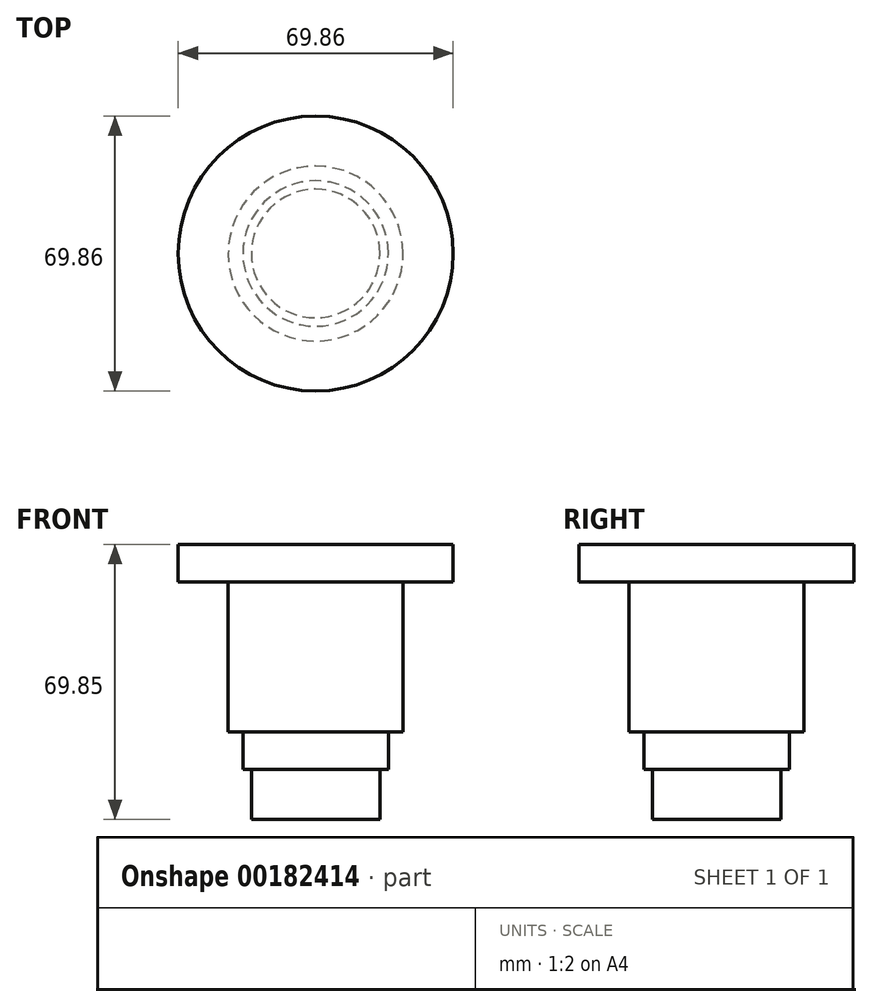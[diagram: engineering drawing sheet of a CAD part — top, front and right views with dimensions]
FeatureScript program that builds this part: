
annotation { "Feature Type Name" : "Feature", "Feature Type Description" : "" }
export const myFeature = defineFeature(function(context is Context, id is Id, definition is map)
    precondition{}
    {
        {
            var Q0;
            Q0=qCreatedBy(makeId("Front.planeOp"),FACE);
            var sketch = newSketch(context, id + "F0", { "sketchPlane" : qUnion([Q0])});
            skLineSegment(sketch, "E0", {"start": v(0, 0) * mm, "end": v(16.33, 0) * mm});
            skLineSegment(sketch, "E1", {"start": v(16.33, 0) * mm, "end": v(16.33, 12.7) * mm});
            skLineSegment(sketch, "E2", {"start": v(16.33, 12.7) * mm, "end": v(18.48, 12.7) * mm});
            skLineSegment(sketch, "E3", {"start": v(18.48, 12.7) * mm, "end": v(18.48, 22.23) * mm});
            skLineSegment(sketch, "E4", {"start": v(18.48, 22.23) * mm, "end": v(22.23, 22.23) * mm});
            skLineSegment(sketch, "E5", {"start": v(22.23, 22.23) * mm, "end": v(22.23, 60.33) * mm});
            skLineSegment(sketch, "E6", {"start": v(22.23, 60.33) * mm, "end": v(34.93, 60.33) * mm});
            skLineSegment(sketch, "E7", {"start": v(34.93, 60.33) * mm, "end": v(34.93, 69.85) * mm});
            skLineSegment(sketch, "E8", {"start": v(34.93, 69.85) * mm, "end": v(0, 69.85) * mm});
            skLineSegment(sketch, "E9", {"start": v(0, 0) * mm, "end": v(0, 69.85) * mm});
            skSolve(sketch);
        }
        {
            var Q0;
            Q0 = qSketchRegion(id + "F0", true);
            var Q1;
            Q1=sQuery(id+"F0.wireOp",EDGE,"E9");
            revolve(context, id + "F1", {"entities" : qUnion([Q0]), "axis" : qUnion([Q1]), "revolveType" : RevolveType.FULL});
        }
    });
